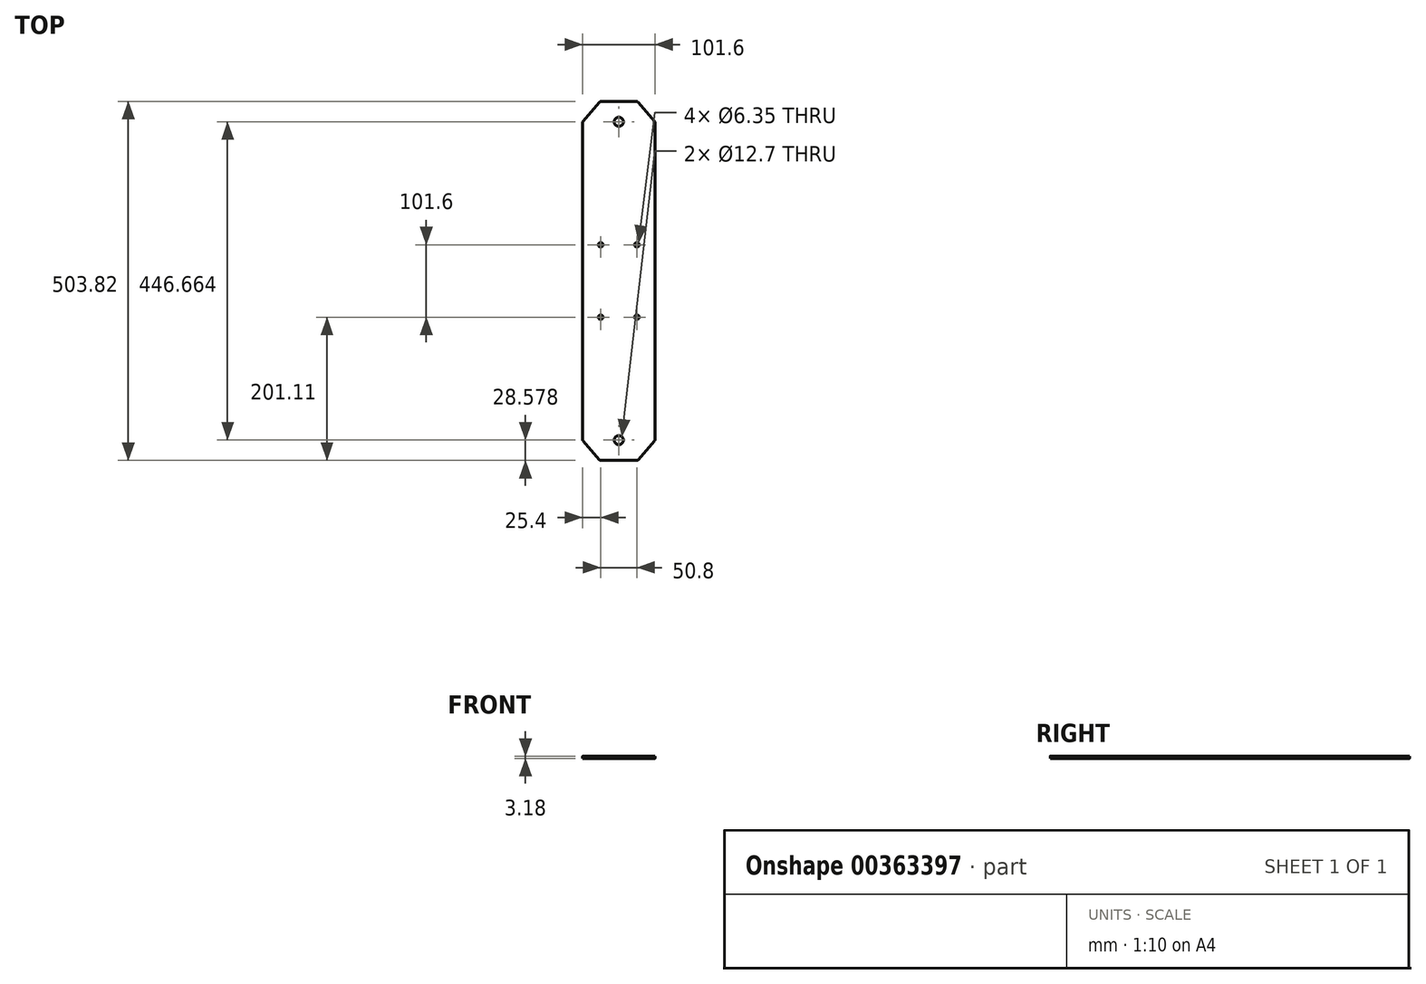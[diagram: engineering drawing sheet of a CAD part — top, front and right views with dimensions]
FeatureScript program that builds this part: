
annotation { "Feature Type Name" : "Feature", "Feature Type Description" : "" }
export const myFeature = defineFeature(function(context is Context, id is Id, definition is map)
    precondition{}
    {
        {
            var Q0;
            Q0=qCreatedBy(makeId("Top.planeOp"),FACE);
            var sketch = newSketch(context, id + "F0", { "sketchPlane" : qUnion([Q0])});
            skLineSegment(sketch, "E0", {"start": v(0, -76.41) * mm, "end": v(0, 88.06) * mm, "construction": true});
            skLineSegment(sketch, "E1", {"start": v(-50.8, 0) * mm, "end": v(-50.8, 222.15) * mm});
            skLineSegment(sketch, "E2", {"start": v(-50.03, 224.23) * mm, "end": v(-27.14, 250.8) * mm});
            skLineSegment(sketch, "E3", {"start": v(-24.73, 251.9) * mm, "end": v(24.73, 251.9) * mm});
            skLineSegment(sketch, "E4", {"start": v(27.14, 250.8) * mm, "end": v(50.03, 224.23) * mm});
            skLineSegment(sketch, "E5", {"start": v(50.8, 222.15) * mm, "end": v(50.8, 0) * mm});
            skLineSegment(sketch, "E6", {"start": v(-76.25, 0) * mm, "end": v(75.88, 0) * mm, "construction": true});
            skCircle(sketch, "E7", {"center": v(0, 223.33) * mm, "radius": 6.35 * mm});
            skLineSegment(sketch, "E8.MirrorCS", {"start": v(-24.73, -251.9) * mm, "end": v(24.73, -251.9) * mm});
            skLineSegment(sketch, "E9.MirrorCS", {"start": v(27.14, -250.8) * mm, "end": v(50.03, -224.23) * mm});
            skLineSegment(sketch, "E10.MirrorCS", {"start": v(-50.03, -224.23) * mm, "end": v(-27.14, -250.8) * mm});
            skLineSegment(sketch, "E11.MirrorCS", {"start": v(-50.8, 0) * mm, "end": v(-50.8, -222.15) * mm});
            skLineSegment(sketch, "E12.MirrorCS", {"start": v(50.8, -222.15) * mm, "end": v(50.8, 0) * mm});
            skCircle(sketch, "E13.MirrorC", {"center": v(0, -223.33) * mm, "radius": 6.35 * mm});
            skPoint(sketch, "E14.visualSharp", {"position": v(-50.8, 223.33) * mm});
            skArc(sketch, "E14.filletArc", {"start": v(-50.03, 224.23) * mm, "mid": v(-50.6, 223.26) * mm, "end": v(-50.8, 222.15) * mm});
            skPoint(sketch, "E15.visualSharp", {"position": v(-26.19, 251.9) * mm});
            skArc(sketch, "E15.filletArc", {"start": v(-24.73, 251.9) * mm, "mid": v(-26.05, 251.62) * mm, "end": v(-27.14, 250.8) * mm});
            skPoint(sketch, "E16.visualSharp", {"position": v(26.19, 251.9) * mm});
            skArc(sketch, "E16.filletArc", {"start": v(27.14, 250.8) * mm, "mid": v(26.05, 251.62) * mm, "end": v(24.73, 251.9) * mm});
            skPoint(sketch, "E17.visualSharp", {"position": v(50.8, 223.33) * mm});
            skArc(sketch, "E17.filletArc", {"start": v(50.8, 222.15) * mm, "mid": v(50.6, 223.26) * mm, "end": v(50.03, 224.23) * mm});
            skPoint(sketch, "E18.visualSharp", {"position": v(50.8, -223.33) * mm});
            skArc(sketch, "E18.filletArc", {"start": v(50.03, -224.23) * mm, "mid": v(50.6, -223.26) * mm, "end": v(50.8, -222.15) * mm});
            skPoint(sketch, "E19.visualSharp", {"position": v(26.19, -251.9) * mm});
            skArc(sketch, "E19.filletArc", {"start": v(24.73, -251.9) * mm, "mid": v(26.05, -251.62) * mm, "end": v(27.14, -250.8) * mm});
            skPoint(sketch, "E20.visualSharp", {"position": v(-26.19, -251.9) * mm});
            skArc(sketch, "E20.filletArc", {"start": v(-27.14, -250.8) * mm, "mid": v(-26.05, -251.62) * mm, "end": v(-24.73, -251.9) * mm});
            skPoint(sketch, "E21.visualSharp", {"position": v(-50.8, -223.33) * mm});
            skArc(sketch, "E21.filletArc", {"start": v(-50.8, -222.15) * mm, "mid": v(-50.6, -223.26) * mm, "end": v(-50.03, -224.23) * mm});
            skLineSegment(sketch, "E22", {"start": v(-50.8, 223.33) * mm, "end": v(50.8, 223.33) * mm, "construction": true});
            skLineSegment(sketch, "E23", {"start": v(-50.8, 88.9) * mm, "end": v(50.8, 88.9) * mm, "construction": true});
            skLineSegment(sketch, "E24.MirrorCS", {"start": v(-50.8, -88.9) * mm, "end": v(50.8, -88.9) * mm, "construction": true});
            skCircle(sketch, "E25", {"center": v(25.4, 50.8) * mm, "radius": 3.18 * mm});
            skCircle(sketch, "E26", {"center": v(-25.4, 50.8) * mm, "radius": 3.18 * mm});
            skLineSegment(sketch, "E27", {"start": v(-25.4, 50.8) * mm, "end": v(25.4, 50.8) * mm, "construction": true});
            skCircle(sketch, "E28.MirrorC", {"center": v(25.4, -50.8) * mm, "radius": 3.18 * mm});
            skCircle(sketch, "E29.MirrorC", {"center": v(-25.4, -50.8) * mm, "radius": 3.18 * mm});
            skSolve(sketch);
        }
        {
            var Q0;
            Q0=makeQuery(id+"F0.imprint","IMPRINT",FACE,{"disambiguationData":[TD([[makeQuery(id+"F0.imprint","IMPRINT",EDGE,{"derivedFrom":sQuery(id+"F0.wireOp",EDGE,"E1")}),-1.0]])]});
            extrude(context, id + "F1", {"entities" : qUnion([Q0]), "depth" : 3.17 * mm});
        }
    });
